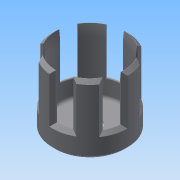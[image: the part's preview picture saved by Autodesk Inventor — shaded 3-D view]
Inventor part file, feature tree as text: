
AUTODESK INVENTOR PART (.ipt)
format: ipt  version: 2015 (Build 190159000, 159)  size: 214,016 bytes
history: native  units: in
note: dims shown in document units (in); Inventor stores cm internally (conversion verified against a paired STEP export)
features: chamfer x3, fillet x3, sketch x2, revolve x1, plane x1, extrude x1, pattern_circular x1
ambient origin geometry x8: Origin, YZ Plane, XZ Plane, XY Plane, X Axis, Y Axis, Z Axis, Center Point
bodies: Solid1 (feature_tree)
feature tree (12):
  revolve  "Revolution1"  [1 undecoded]
  chamfer  "Chamfer1"  Distance=0.2953in
  fillet  "Fillet1"  Radius=0.1378in
  fillet  "Fillet2"  [1 undecoded]
  plane  "Work Plane1"
  chamfer  "Chamfer2"  Distance=0.0295in Angle=45.0deg
  extrude  "Extrusion2"  Depth=2.0in
  chamfer  "Chamfer3"  Distance=0.1in
  fillet  "Fillet3"  Radius=0.1in
  pattern_circular  "Circular Pattern1"  [2 undecoded]
  sketch  "Sketch1"  dims[d0=0.9961in d1=1.9291in]
  sketch  "Sketch3"  dims[d2=0.1378in d3=0.2953in d4=0.1378in d5=90.0deg d6=0.0295in d7=0.125in d8=45.0deg d9=2.0in d10=0.1in d11=0.1in d12=0.125in d13=45.0deg d17=0.1718in d18=1.0in d19=0.0in d20=0.5512in d21=2.3622in d22=360.0deg d24=0.1in d25=0.125in d26=45.0deg d27=0.025in]
note: 4 required parameter values undecoded (feature->parameter linkage not recoverable at this tier; creation-order binding heuristic only, values carry confidence <= 0.55)